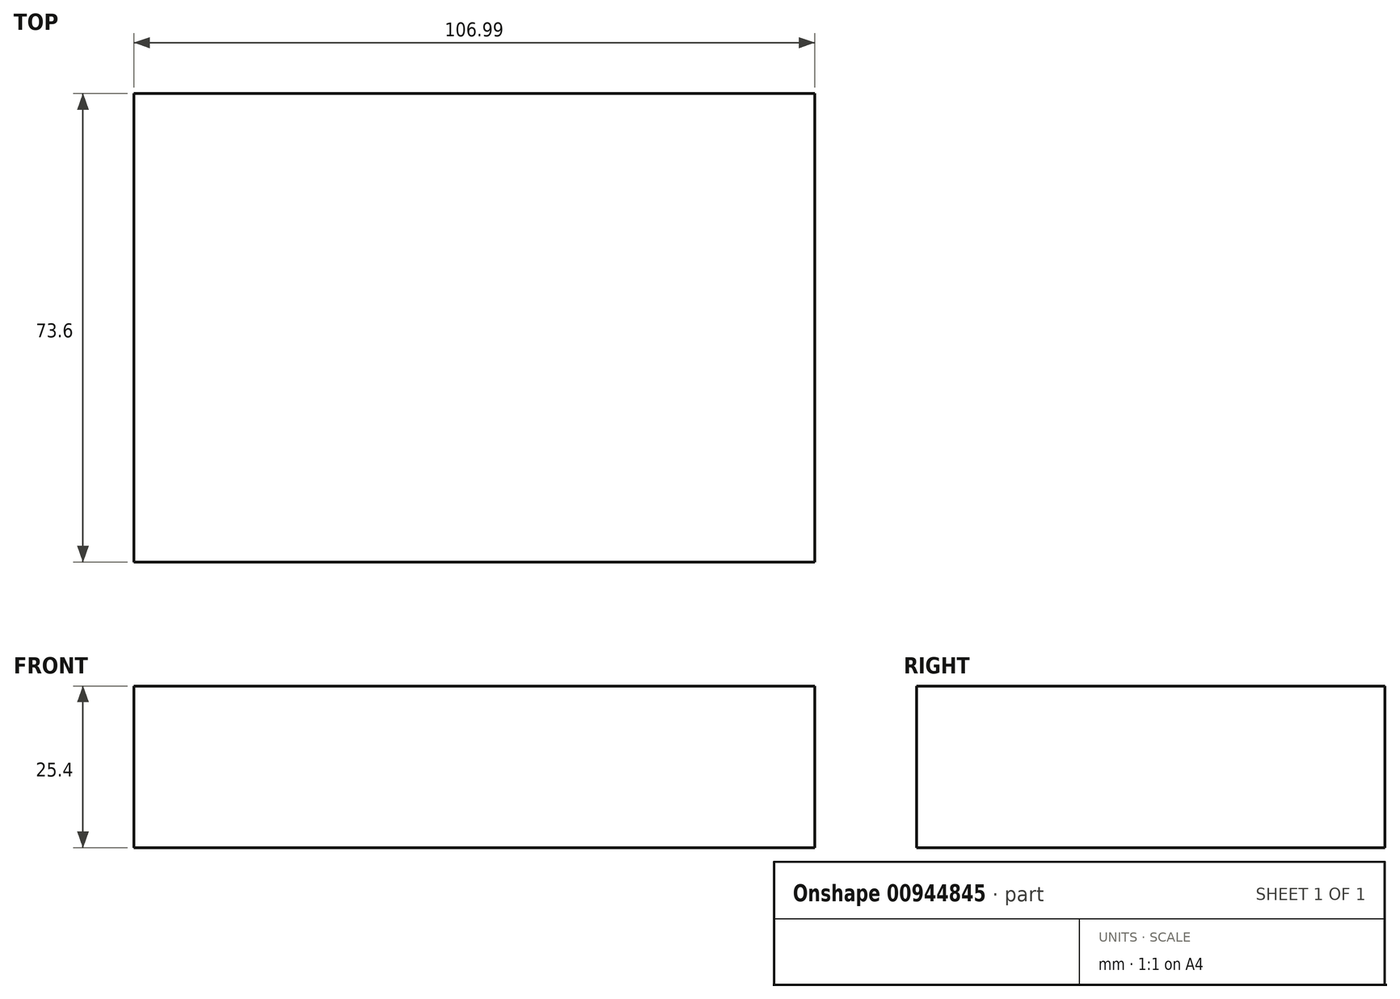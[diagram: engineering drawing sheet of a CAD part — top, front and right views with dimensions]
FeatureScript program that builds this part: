
annotation { "Feature Type Name" : "Feature", "Feature Type Description" : "" }
export const myFeature = defineFeature(function(context is Context, id is Id, definition is map)
    precondition{}
    {
        {
            var Q0;
            Q0=qCreatedBy(makeId("Top.planeOp"),FACE);
            var sketch = newSketch(context, id + "F0", { "sketchPlane" : qUnion([Q0])});
            skLineSegment(sketch, "E0.bottom", {"start": v(-46.8, 35.85) * mm, "end": v(60.2, 35.85) * mm});
            skLineSegment(sketch, "E0.top", {"start": v(-46.8, -37.75) * mm, "end": v(60.2, -37.75) * mm});
            skLineSegment(sketch, "E0.left", {"start": v(-46.8, 35.85) * mm, "end": v(-46.8, -37.75) * mm});
            skLineSegment(sketch, "E0.right", {"start": v(60.2, 35.85) * mm, "end": v(60.2, -37.75) * mm});
            skSolve(sketch);
        }
        {
            var Q0;
            Q0=makeQuery(id+"F0.imprint","IMPRINT",FACE,{"disambiguationData":[TD([[makeQuery(id+"F0.imprint","IMPRINT",EDGE,{"derivedFrom":sQuery(id+"F0.wireOp",EDGE,"E0.bottom")}),-1.0]])]});
            extrude(context, id + "F1", {"entities" : qUnion([Q0]), "depth" : 25.4 * mm, "offsetDistance" : 25.4 * mm});
        }
    });
